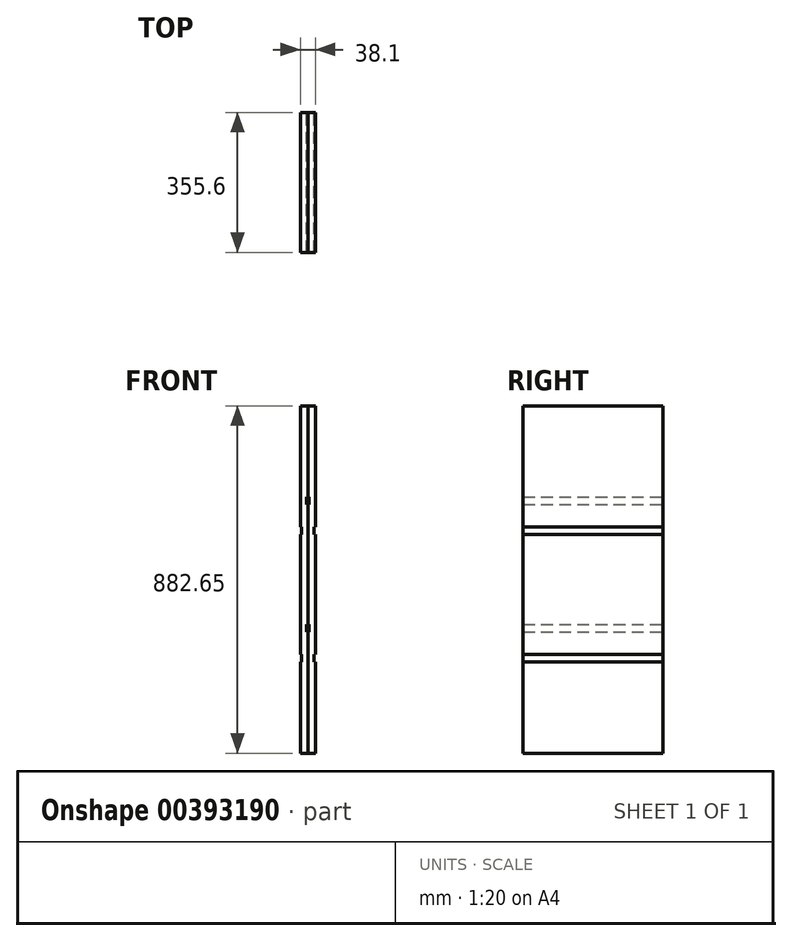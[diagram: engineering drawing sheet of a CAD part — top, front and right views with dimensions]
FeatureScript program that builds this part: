
annotation { "Feature Type Name" : "Feature", "Feature Type Description" : "" }
export const myFeature = defineFeature(function(context is Context, id is Id, definition is map)
    precondition{}
    {
        {
            var Q0;
            Q0=qCreatedBy(makeId("Right.planeOp"),FACE);
            var sketch = newSketch(context, id + "F0", { "sketchPlane" : qUnion([Q0])});
            skLineSegment(sketch, "E0.bottom", {"start": v(-774.77, 478) * mm, "end": v(-419.17, 478) * mm});
            skLineSegment(sketch, "E0.top", {"start": v(-774.77, -404.66) * mm, "end": v(-419.17, -404.66) * mm});
            skLineSegment(sketch, "E0.left", {"start": v(-774.77, 478) * mm, "end": v(-774.77, -404.66) * mm});
            skLineSegment(sketch, "E0.right", {"start": v(-419.17, 478) * mm, "end": v(-419.17, -404.66) * mm});
            skLineSegment(sketch, "E1.bottom", {"start": v(-774.77, 246.22) * mm, "end": v(-419.17, 246.22) * mm});
            skLineSegment(sketch, "E1.top", {"start": v(-774.77, 227.17) * mm, "end": v(-419.17, 227.17) * mm});
            skLineSegment(sketch, "E1.left", {"start": v(-774.77, 246.22) * mm, "end": v(-774.77, 227.17) * mm});
            skLineSegment(sketch, "E1.right", {"start": v(-419.17, 246.22) * mm, "end": v(-419.17, 227.17) * mm});
            skLineSegment(sketch, "E2.MirrorCS", {"start": v(-774.77, -77.63) * mm, "end": v(-419.17, -77.63) * mm});
            skLineSegment(sketch, "E3.MirrorCS", {"start": v(-774.77, -96.68) * mm, "end": v(-419.17, -96.68) * mm});
            skSolve(sketch);
        }
        {
            var Q0;
            Q0=makeQuery(id+"F0.imprint","IMPRINT",FACE,{"disambiguationData":[TD([[makeQuery(id+"F0.imprint","IMPRINT",EDGE,{"derivedFrom":sQuery(id+"F0.wireOp",EDGE,"E1.bottom")}),-1.0]])]});
            var Q1;
            {var subQ0=sQuery(id+"F0.wireOp",EDGE,"E2.MirrorCS");Q1=makeQuery(id+"F0.imprint","IMPRINT",FACE,{"disambiguationData":[TD([[makeQuery(id+"F0.imprint","IMPRINT",EDGE,{"derivedFrom":subQ0}),-1.0]])]});}
            var Q2;
            {var subQ0=sQuery(id+"F0.wireOp",EDGE,"E0.bottom");Q2=makeQuery(id+"F0.imprint","IMPRINT",FACE,{"disambiguationData":[TD([[makeQuery(id+"F0.imprint","IMPRINT",EDGE,{"derivedFrom":subQ0}),-1.0]])]});}
            var Q3;
            {var subQ0=sQuery(id+"F0.wireOp",EDGE,"E0.top");Q3=makeQuery(id+"F0.imprint","IMPRINT",FACE,{"disambiguationData":[TD([[makeQuery(id+"F0.imprint","IMPRINT",EDGE,{"derivedFrom":subQ0}),1.0]])]});}
            var Q4;
            {var subQ0=sQuery(id+"F0.wireOp",EDGE,"E1.top");Q4=makeQuery(id+"F0.imprint","IMPRINT",FACE,{"disambiguationData":[TD([[makeQuery(id+"F0.imprint","IMPRINT",EDGE,{"derivedFrom":subQ0}),-1.0]])]});}
            var Q5;
            Q5=sQuery(id+"F0.wireOp",EDGE,"E0.left");
            var Q6;
            Q6=sQuery(id+"F0.wireOp",EDGE,"E2.MirrorCS");
            var Q7;
            Q7=sQuery(id+"F0.wireOp",EDGE,"E3.MirrorCS");
            var Q8;
            Q8=sQuery(id+"F0.wireOp",EDGE,"E1.top");
            var Q9;
            Q9=sQuery(id+"F0.wireOp",EDGE,"E0.top");
            var Q10;
            Q10=sQuery(id+"F0.wireOp",EDGE,"E1.bottom");
            var Q11;
            Q11=sQuery(id+"F0.wireOp",EDGE,"E0.bottom");
            var Q12;
            Q12=sQuery(id+"F0.wireOp",EDGE,"E0.right");
            var Q13;
            Q13=sQuery(id+"F0.wireOp",EDGE,"E1.left");
            var Q14;
            Q14=sQuery(id+"F0.wireOp",EDGE,"E1.right");
            extrude(context, id + "F1", {"entities" : qUnion([Q0, Q1, Q2, Q3, Q4]), "surfaceEntities" : qUnion([Q5, Q6, Q7, Q8, Q9, Q10, Q11, Q12, Q13, Q14]), "depth" : 19.05 * mm});
        }
        {
            var Q0;
            Q0=makeQuery(id+"F0.imprint","IMPRINT",FACE,{"disambiguationData":[TD([[makeQuery(id+"F0.imprint","IMPRINT",EDGE,{"derivedFrom":sQuery(id+"F0.wireOp",EDGE,"E1.bottom")}),-1.0]])]});
            var Q1;
            {var subQ0=sQuery(id+"F0.wireOp",EDGE,"E2.MirrorCS");Q1=makeQuery(id+"F0.imprint","IMPRINT",FACE,{"disambiguationData":[TD([[makeQuery(id+"F0.imprint","IMPRINT",EDGE,{"derivedFrom":subQ0}),-1.0]])]});}
            extrude(context, id + "F2", {"entities" : qUnion([Q0, Q1]), "operationType" : NewBodyOperationType.REMOVE, "depth" : 3.17 * mm});
        }
        {
            var Q0;
            Q0=makeQuery(id+"F1.opExtrude","CAP_FACE",FACE,{"disambiguationData":[OSD([sQuery(id+"F0.wireOp",EDGE,"E0.bottom"),sQuery(id+"F0.wireOp",EDGE,"E0.top"),sQuery(id+"F0.wireOp",EDGE,"E0.left"),sQuery(id+"F0.wireOp",EDGE,"E0.right"),sQuery(id+"F0.wireOp",EDGE,"E1.left"),sQuery(id+"F0.wireOp",EDGE,"E1.right")])],"isStart":false});
            var sketch = newSketch(context, id + "F3", { "sketchPlane" : qUnion([Q0])});
            skLineSegment(sketch, "E4.bottom", {"start": v(-774.77, 170.02) * mm, "end": v(-419.17, 170.02) * mm});
            skLineSegment(sketch, "E4.top", {"start": v(-774.77, 150.97) * mm, "end": v(-419.17, 150.97) * mm});
            skLineSegment(sketch, "E4.left", {"start": v(-774.77, 170.02) * mm, "end": v(-774.77, 150.97) * mm});
            skLineSegment(sketch, "E4.right", {"start": v(-419.17, 170.02) * mm, "end": v(-419.17, 150.97) * mm});
            skLineSegment(sketch, "E5.MirrorCS", {"start": v(-774.77, -153.83) * mm, "end": v(-419.17, -153.83) * mm});
            skLineSegment(sketch, "E6.MirrorCS", {"start": v(-774.77, -172.88) * mm, "end": v(-419.17, -172.88) * mm});
            skSolve(sketch);
        }
        {
            var Q0;
            Q0 = qSketchRegion(id + "F3", true);
            var Q1;
            {var subQ0=sQuery(id+"F3.wireOp",EDGE,"E5.MirrorCS");Q1=makeQuery(id+"F3.imprint","IMPRINT",FACE,{"disambiguationData":[TD([[makeQuery(id+"F3.imprint","IMPRINT",EDGE,{"derivedFrom":subQ0}),-1.0]])]});}
            extrude(context, id + "F4", {"entities" : qUnion([Q0, Q1]), "operationType" : NewBodyOperationType.REMOVE, "oppositeDirection" : true, "depth" : 3.17 * mm});
        }
        {
            var Q0;
            Q0=makeQuery(id+"F1.opExtrude","SWEPT_BODY",BODY,{"disambiguationData":[OSD([sQuery(id+"F0.wireOp",EDGE,"E0.bottom"),sQuery(id+"F0.wireOp",EDGE,"E0.top"),sQuery(id+"F0.wireOp",EDGE,"E0.left"),sQuery(id+"F0.wireOp",EDGE,"E0.right"),sQuery(id+"F0.wireOp",EDGE,"E1.left"),sQuery(id+"F0.wireOp",EDGE,"E1.right")])]});
            var Q1;
            Q1=qCreatedBy(makeId("Right.planeOp"),FACE);
            mirror(context, id + "F5", {"entities" : qUnion([Q0]), "mirrorPlane" : qUnion([Q1])});
        }
    });
